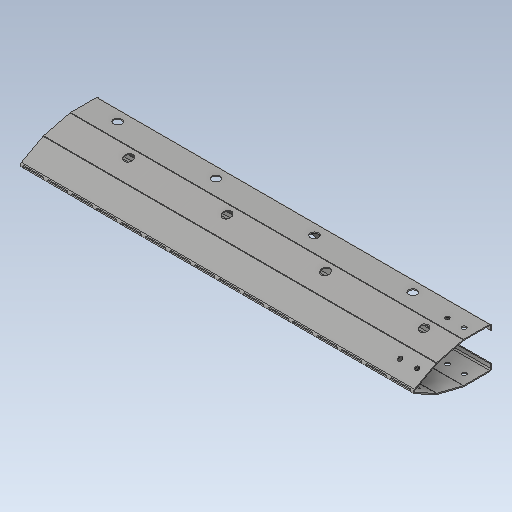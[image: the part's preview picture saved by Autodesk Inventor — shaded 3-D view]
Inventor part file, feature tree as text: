
AUTODESK INVENTOR PART (.ipt)
format: ipt  version: 2020.1 (Build 241239000, 239)  size: 889,856 bytes
history: native  units: mm
features: reference x25, other x24, sketch x23, hole x16, sheet_metal_op x13, plane x9, projected_geometry x7, extrude x4
ambient origin geometry x8: Origin, YZ Plane, XZ Plane, XY Plane, X Axis, Y Axis, Z Axis, Center Point
bodies: Solid1 (feature_tree)
feature tree (121):
  plane  "Work Plane1"
  sheet_metal_op  "Face1"
  plane  "Work Plane2"
  sheet_metal_op  "Face2"
  plane  "Work Plane3"
  sheet_metal_op  "Face3"
  plane  "Work Plane4"
  sheet_metal_op  "Face4"
  plane  "Work Plane5"
  sheet_metal_op  "Face5"
  plane  "Work Plane6"
  sheet_metal_op  "Face6"
  plane  "Work Plane7"
  sheet_metal_op  "Face7"
  other  "midtplan"
  extrude  "Extrusion3"  Depth=3.75mm
  extrude  "hulsæt til stifter"  Depth=3.0mm
  plane  "Work Plane11"
  sketch  "Sketch13"  dims[d18=1.5mm d19=6.0mm]
  plane  "Work Plane12"
  extrude  "balusterhul"  Depth=3.75mm
  extrude  "balusterhul skråkompensering"  Depth=3.0mm
  hole  "Hole2"  [1 undecoded]
  hole  "Hole4"  [1 undecoded]
  hole  "Hole6"  [1 undecoded]
  hole  "Hole8"  [1 undecoded]
  hole  "Hole10"  [1 undecoded]
  hole  "Hole12"  [1 undecoded]
  hole  "Hole14"  [1 undecoded]
  hole  "Hole16"  [1 undecoded]
  sketch  "Sketch1"  dims[d0=3.0mm d1=3.75mm]
  reference  "Reference1"
  reference  "Reference2"
  reference  "Reference3"
  reference  "Reference4"
  other  "Plate1"
  sketch  "Sketch2"  dims[d2=3.0mm d3=1.5mm]
  reference  "Reference5"
  reference  "Reference6"
  reference  "Reference7"
  reference  "Reference8"
  other  "Plate2"
  sheet_metal_op  "Bend1"
  sketch  "Sketch3"  dims[d4=6.0mm d5=3.75mm]
  reference  "Reference9"
  reference  "Reference10"
  reference  "Reference11"
  other  "Plate3"
  sheet_metal_op  "Bend2"
  sketch  "Sketch4"  dims[d6=3.75mm d7=3.0mm]
  reference  "Reference12"
  reference  "Reference13"
  reference  "Reference14"
  reference  "Reference15"
  other  "Plate4"
  sheet_metal_op  "Bend3"
  sketch  "Sketch5"  dims[d8=1.5mm d9=6.0mm]
  reference  "Reference16"
  reference  "Reference17"
  reference  "Reference18"
  other  "Plate5"
  sheet_metal_op  "Bend4"
  sketch  "Sketch6"  dims[d10=3.75mm d11=3.75mm]
  reference  "Reference19"
  reference  "Reference20"
  reference  "Reference21"
  other  "Plate6"
  sheet_metal_op  "Bend5"
  sketch  "Sketch7"  dims[d12=3.0mm d13=1.5mm]
  reference  "Reference22"
  reference  "Reference23"
  other  "Plate7"
  sheet_metal_op  "Bend6"
  sketch  "Sketch8"  dims[d14=6.0mm d15=3.75mm]
  reference  "Reference24"
  projected_geometry  "Projected Loop1"
  other  "huller til stifter"
  projected_geometry  "Projected Loop3"
  sketch  "Sketch12"  dims[d16=3.75mm d17=3.0mm]
  projected_geometry  "Projected Loop4"
  reference  "Reference25"
  sketch  "Sketch14"  dims[d20=3.75mm d21=3.75mm]
  sketch  "Sketch15"  dims[d22=3.0mm d23=1.5mm]
  projected_geometry  "Projected Loop5"
  projected_geometry  "Projected Loop6"
  sketch  "Sketch16"  dims[d24=6.0mm d25=3.75mm]
  projected_geometry  "Projected Loop7"
  projected_geometry  "Projected Loop8"
  sketch  "Sketch17"  dims[d26=3.75mm d27=3.0mm]
  sketch  "Sketch18"  dims[d28=1.5mm d29=6.0mm]
  hole  "Hole1"  [1 undecoded]
  sketch  "Sketch19"  dims[d30=3.75mm d31=3.0mm]
  hole  "Hole3"  [1 undecoded]
  sketch  "Sketch20"  dims[d32=0.0mm d33=3.0mm]
  hole  "Hole5"  [1 undecoded]
  sketch  "Sketch21"  dims[d39=250.0mm d41=33.7mm]
  hole  "Hole7"  [1 undecoded]
  sketch  "Sketch22"  dims[d42=33.7mm d43=60.0mm d44=60.0mm]
  hole  "Hole9"  [1 undecoded]
  sketch  "Sketch23"  dims[d45=16.85mm d46=65.0mm]
  hole  "Hole11"  [1 undecoded]
  sketch  "Sketch24"  dims[d47=60.0mm]
  hole  "Hole13"  [1 undecoded]
  sketch  "Sketch25"  dims[d48=10.0mm d49=0.0mm]
  hole  "Hole15"  [1 undecoded]
  sketch  "Sketch26"  dims[d68=291.052mm d69=10.0mm d70=0.0mm d73=96.672mm d77=39.001254mm d78=26.6mm d79=25.8mm d80=40.0mm d82=302.737mm d83=10.0mm d85=10.0mm d87=302.737mm d88=113.655385mm d89=56.827692mm d90=90.0deg d91=90.0deg d92=49.5mm d93=100.0mm d94=0.0mm d97=2.046461mm d98=1.023231mm d99=10.0mm d100=0.0mm d101=90.0mm d102=30.0mm d103=522.678194mm d104=342.992513mm d106=342.992513mm d107=30.0mm d108=30.0mm d109=342.992513mm d110=30.0mm d111=342.992513mm d112=624.299345mm d113=10.0mm d114=3.0mm d115=0.0mm d116=221.306832mm d117=119.685681mm d118=96.672222mm d119=61.97046mm d120=1208.948mm d121=8.0mm d122=62.8mm d123=6.0mm d124=170.0mm d126=75.36mm d127=10.0mm d129=10.0mm d131=3.0mm d132=0.0mm d133=12.56mm d134=13.5mm d135=6.0mm d136=4.0mm d137=2.0mm d138=90.0deg d139=8.0mm d140=0.0mm d141=13.5mm d142=6.0mm d143=4.0mm d144=2.0mm d145=90.0deg d146=8.0mm d147=0.0mm d148=13.5mm d149=6.0mm d150=4.0mm d151=2.0mm d152=90.0deg d153=8.0mm d154=0.0mm d155=13.5mm d156=6.0mm d157=4.0mm d158=2.0mm d159=90.0deg d160=8.0mm d161=0.0mm d162=13.5mm d163=6.0mm d164=4.0mm d165=2.0mm d166=90.0deg d167=8.0mm d168=0.0mm d169=13.5mm d170=6.0mm d171=4.0mm d172=2.0mm d173=90.0deg d174=8.0mm d175=0.0mm d176=13.5mm d177=6.0mm d178=4.0mm d179=2.0mm d180=90.0deg d181=8.0mm d182=0.0mm d183=13.5mm d184=6.0mm d185=4.0mm d186=2.0mm d187=90.0deg d188=8.0mm d189=0.0mm d190=1.0mm d191=1.0mm d192=140.0mm d193=3.0mm d194=0.0mm]
  other  "Cut1"
  other  "plantehuller"
  other  "bukkeperforering"
  other  "test af laskehuller"
  parser-record x4  (decoder bookkeeping rows leaked as tree rows — omitted from the tree; the rows remain in map.json)
  other  "modul.iam"
  other  "model:1"
  other  "Definition1"
  other  "søjle+vange.iam"
  other  "modul top:1"
  other  "vange top:1"
  other  "modul top.iam"
note: 16 required parameter values undecoded (feature->parameter linkage not recoverable at this tier; creation-order binding heuristic only, values carry confidence <= 0.55)
note: 4 file-system paths scrubbed to <path> (originals preserved in map.json)
